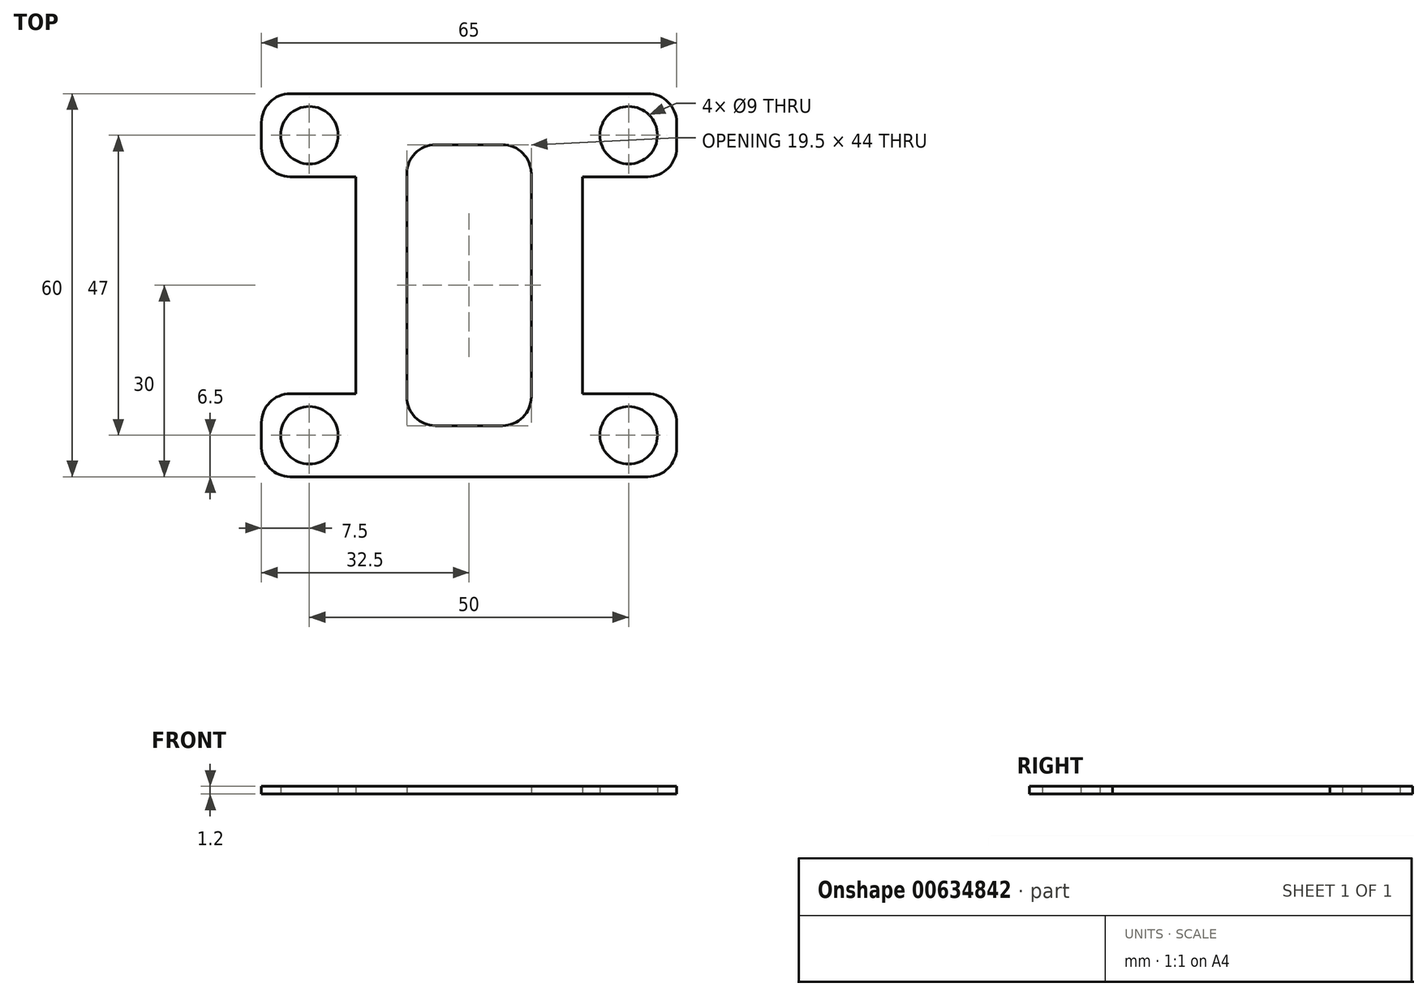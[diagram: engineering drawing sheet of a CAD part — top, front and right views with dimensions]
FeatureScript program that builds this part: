
annotation { "Feature Type Name" : "Feature", "Feature Type Description" : "" }
export const myFeature = defineFeature(function(context is Context, id is Id, definition is map)
    precondition{}
    {
        {
            var Q0;
            Q0=qCreatedBy(makeId("Top.planeOp"),FACE);
            var sketch = newSketch(context, id + "F0", { "sketchPlane" : qUnion([Q0])});
            skLineSegment(sketch, "E0.bottom", {"start": v(17.75, 30) * mm, "end": v(-17.75, 30) * mm});
            skLineSegment(sketch, "E0.top", {"start": v(17.75, -30) * mm, "end": v(-17.75, -30) * mm});
            skLineSegment(sketch, "E0.left", {"start": v(17.75, 30) * mm, "end": v(17.75, -30) * mm});
            skLineSegment(sketch, "E0.right", {"start": v(-17.75, 30) * mm, "end": v(-17.75, -30) * mm});
            skPoint(sketch, "E0.middle", {"position": v(0, 0) * mm});
            skCircle(sketch, "E1", {"center": v(25, 23.5) * mm, "radius": 4.5 * mm});
            skCircle(sketch, "E2.MirrorC", {"center": v(25, -23.5) * mm, "radius": 4.5 * mm});
            skCircle(sketch, "E3.MirrorC", {"center": v(-25, 23.5) * mm, "radius": 4.5 * mm});
            skCircle(sketch, "E4.MirrorC", {"center": v(-25, -23.5) * mm, "radius": 4.5 * mm});
            skLineSegment(sketch, "E5.bottom", {"start": v(-28, 30) * mm, "end": v(28, 30) * mm});
            skLineSegment(sketch, "E5.top", {"start": v(-28, 17) * mm, "end": v(28, 17) * mm});
            skLineSegment(sketch, "E5.left", {"start": v(-32.5, 25.5) * mm, "end": v(-32.5, 21.5) * mm});
            skLineSegment(sketch, "E5.right", {"start": v(32.5, 25.5) * mm, "end": v(32.5, 21.5) * mm});
            skPoint(sketch, "E6.visualSharp", {"position": v(-32.5, 30) * mm});
            skArc(sketch, "E6.filletArc", {"start": v(-28, 30) * mm, "mid": v(-31.18, 28.68) * mm, "end": v(-32.5, 25.5) * mm});
            skPoint(sketch, "E7.visualSharp", {"position": v(-32.5, 17) * mm});
            skArc(sketch, "E7.filletArc", {"start": v(-32.5, 21.5) * mm, "mid": v(-31.18, 18.32) * mm, "end": v(-28, 17) * mm});
            skPoint(sketch, "E8.visualSharp", {"position": v(32.5, 30) * mm});
            skArc(sketch, "E8.filletArc", {"start": v(32.5, 25.5) * mm, "mid": v(31.18, 28.68) * mm, "end": v(28, 30) * mm});
            skPoint(sketch, "E9.visualSharp", {"position": v(32.5, 17) * mm});
            skArc(sketch, "E9.filletArc", {"start": v(28, 17) * mm, "mid": v(31.18, 18.32) * mm, "end": v(32.5, 21.5) * mm});
            skLineSegment(sketch, "E10.MirrorCS", {"start": v(-28, -17) * mm, "end": v(28, -17) * mm});
            skArc(sketch, "E11.MirrorCS", {"start": v(-32.5, -21.5) * mm, "mid": v(-31.18, -18.32) * mm, "end": v(-28, -17) * mm});
            skLineSegment(sketch, "E12.MirrorCS", {"start": v(-32.5, -25.5) * mm, "end": v(-32.5, -21.5) * mm});
            skArc(sketch, "E13.MirrorCS", {"start": v(-28, -30) * mm, "mid": v(-31.18, -28.68) * mm, "end": v(-32.5, -25.5) * mm});
            skLineSegment(sketch, "E14.MirrorCS", {"start": v(-28, -30) * mm, "end": v(28, -30) * mm});
            skArc(sketch, "E15.MirrorCS", {"start": v(32.5, -25.5) * mm, "mid": v(31.18, -28.68) * mm, "end": v(28, -30) * mm});
            skLineSegment(sketch, "E16.MirrorCS", {"start": v(32.5, -25.5) * mm, "end": v(32.5, -21.5) * mm});
            skArc(sketch, "E17.MirrorCS", {"start": v(28, -17) * mm, "mid": v(31.18, -18.32) * mm, "end": v(32.5, -21.5) * mm});
            skLineSegment(sketch, "E18.bottom", {"start": v(5.25, 22) * mm, "end": v(-5.25, 22) * mm});
            skLineSegment(sketch, "E18.top", {"start": v(5.25, -22) * mm, "end": v(-5.25, -22) * mm});
            skLineSegment(sketch, "E18.left", {"start": v(9.75, 17.5) * mm, "end": v(9.75, -17.5) * mm});
            skLineSegment(sketch, "E18.right", {"start": v(-9.75, 17.5) * mm, "end": v(-9.75, -17.5) * mm});
            skPoint(sketch, "E19.visualSharp", {"position": v(-9.75, 22) * mm});
            skArc(sketch, "E19.filletArc", {"start": v(-5.25, 22) * mm, "mid": v(-8.43, 20.68) * mm, "end": v(-9.75, 17.5) * mm});
            skPoint(sketch, "E20.visualSharp", {"position": v(9.75, 22) * mm});
            skArc(sketch, "E20.filletArc", {"start": v(9.75, 17.5) * mm, "mid": v(8.43, 20.68) * mm, "end": v(5.25, 22) * mm});
            skPoint(sketch, "E21.visualSharp", {"position": v(9.75, -22) * mm});
            skArc(sketch, "E21.filletArc", {"start": v(5.25, -22) * mm, "mid": v(8.43, -20.68) * mm, "end": v(9.75, -17.5) * mm});
            skPoint(sketch, "E22.visualSharp", {"position": v(-9.75, -22) * mm});
            skArc(sketch, "E22.filletArc", {"start": v(-9.75, -17.5) * mm, "mid": v(-8.43, -20.68) * mm, "end": v(-5.25, -22) * mm});
            skSolve(sketch);
        }
        {
            var Q0;
            Q0 = qSketchRegion(id + "F0", true);
            extrude(context, id + "F1", {"entities" : qUnion([Q0]), "depth" : 1.2 * mm, "offsetDistance" : 25 * mm});
        }
    });
